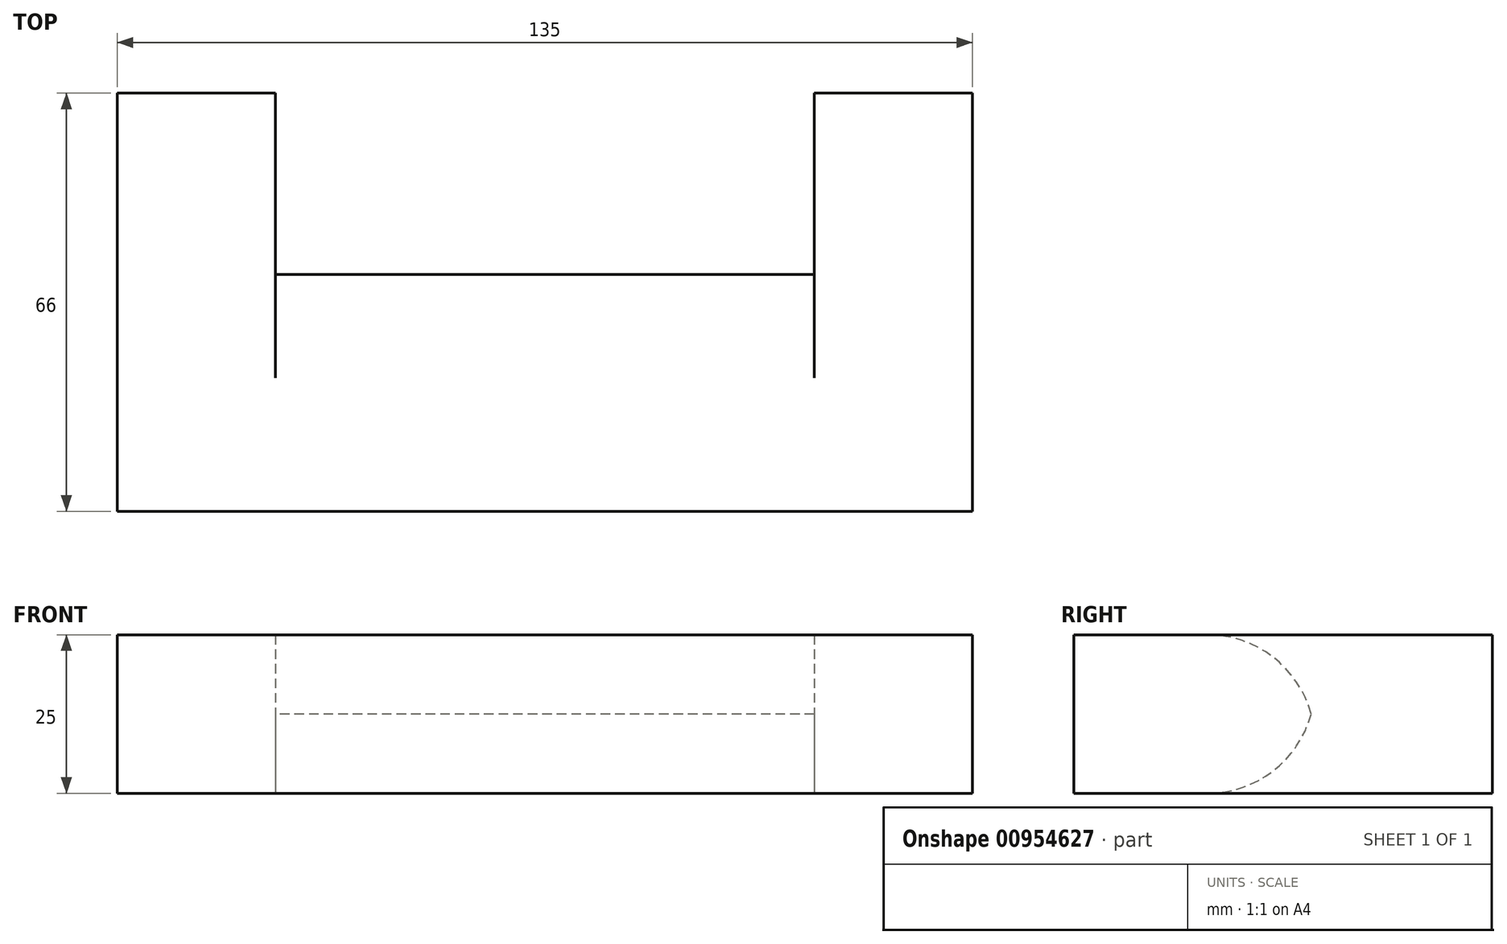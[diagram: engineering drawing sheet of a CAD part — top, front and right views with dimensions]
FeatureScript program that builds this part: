
annotation { "Feature Type Name" : "Feature", "Feature Type Description" : "" }
export const myFeature = defineFeature(function(context is Context, id is Id, definition is map)
    precondition{}
    {
        {
            var Q0;
            Q0=qCreatedBy(makeId("Front.planeOp"),FACE);
            var sketch = newSketch(context, id + "F0", { "sketchPlane" : qUnion([Q0])});
            skLineSegment(sketch, "E0.bottom", {"start": v(0, 0) * mm, "end": v(135, 0) * mm});
            skLineSegment(sketch, "E0.top", {"start": v(0, -25) * mm, "end": v(135, -25) * mm});
            skLineSegment(sketch, "E0.left", {"start": v(0, 0) * mm, "end": v(0, -25) * mm});
            skLineSegment(sketch, "E0.right", {"start": v(135, 0) * mm, "end": v(135, -25) * mm});
            skSolve(sketch);
        }
        {
            var Q0;
            Q0 = qSketchRegion(id + "F0", true);
            extrude(context, id + "F1", {"entities" : qUnion([Q0]), "depth" : 38 * mm, "offsetDistance" : 25 * mm});
        }
        {
            var Q0;
            Q0=makeQuery(id+"F1.opExtrude","CAP_FACE",FACE,{"disambiguationData":[OSD([sQuery(id+"F0.wireOp",EDGE,"E0.bottom"),sQuery(id+"F0.wireOp",EDGE,"E0.top"),sQuery(id+"F0.wireOp",EDGE,"E0.left"),sQuery(id+"F0.wireOp",EDGE,"E0.right")])],"isStart":true});
            var sketch = newSketch(context, id + "F2", { "sketchPlane" : qUnion([Q0])});
            skLineSegment(sketch, "E1.bottom", {"start": v(-135, 0) * mm, "end": v(-110, 0) * mm});
            skLineSegment(sketch, "E1.top", {"start": v(-135, -25) * mm, "end": v(-110, -25) * mm});
            skLineSegment(sketch, "E1.left", {"start": v(-135, 0) * mm, "end": v(-135, -25) * mm});
            skLineSegment(sketch, "E1.right", {"start": v(-110, 0) * mm, "end": v(-110, -25) * mm});
            skLineSegment(sketch, "E2.bottom", {"start": v(0, 0) * mm, "end": v(-25, 0) * mm});
            skLineSegment(sketch, "E2.top", {"start": v(0, -25) * mm, "end": v(-25, -25) * mm});
            skLineSegment(sketch, "E2.left", {"start": v(0, 0) * mm, "end": v(0, -25) * mm});
            skLineSegment(sketch, "E2.right", {"start": v(-25, 0) * mm, "end": v(-25, -25) * mm});
            skSolve(sketch);
        }
        {
            var Q0;
            Q0 = qSketchRegion(id + "F2", true);
            extrude(context, id + "F3", {"entities" : qUnion([Q0]), "operationType" : NewBodyOperationType.ADD, "depth" : 28 * mm, "offsetDistance" : 25 * mm});
        }
        {
            var Q0;
            Q0=makeQuery(id+"F1.opExtrude","CAP_EDGE",EDGE,{"disambiguationData":[OSD([sQuery(id+"F0.wireOp",EDGE,"E0.bottom")])],"isStart":true});
            var Q1;
            Q1=makeQuery(id+"F1.opExtrude","CAP_EDGE",EDGE,{"disambiguationData":[OSD([sQuery(id+"F0.wireOp",EDGE,"E0.top")])],"isStart":true});
            fillet(context, id + "F4", {"entities" : qUnion([Q0, Q1]), "radius" : 16.9 * mm, "tangentPropagation" : true, "allowEdgeOverflow" : false});
        }
    });
